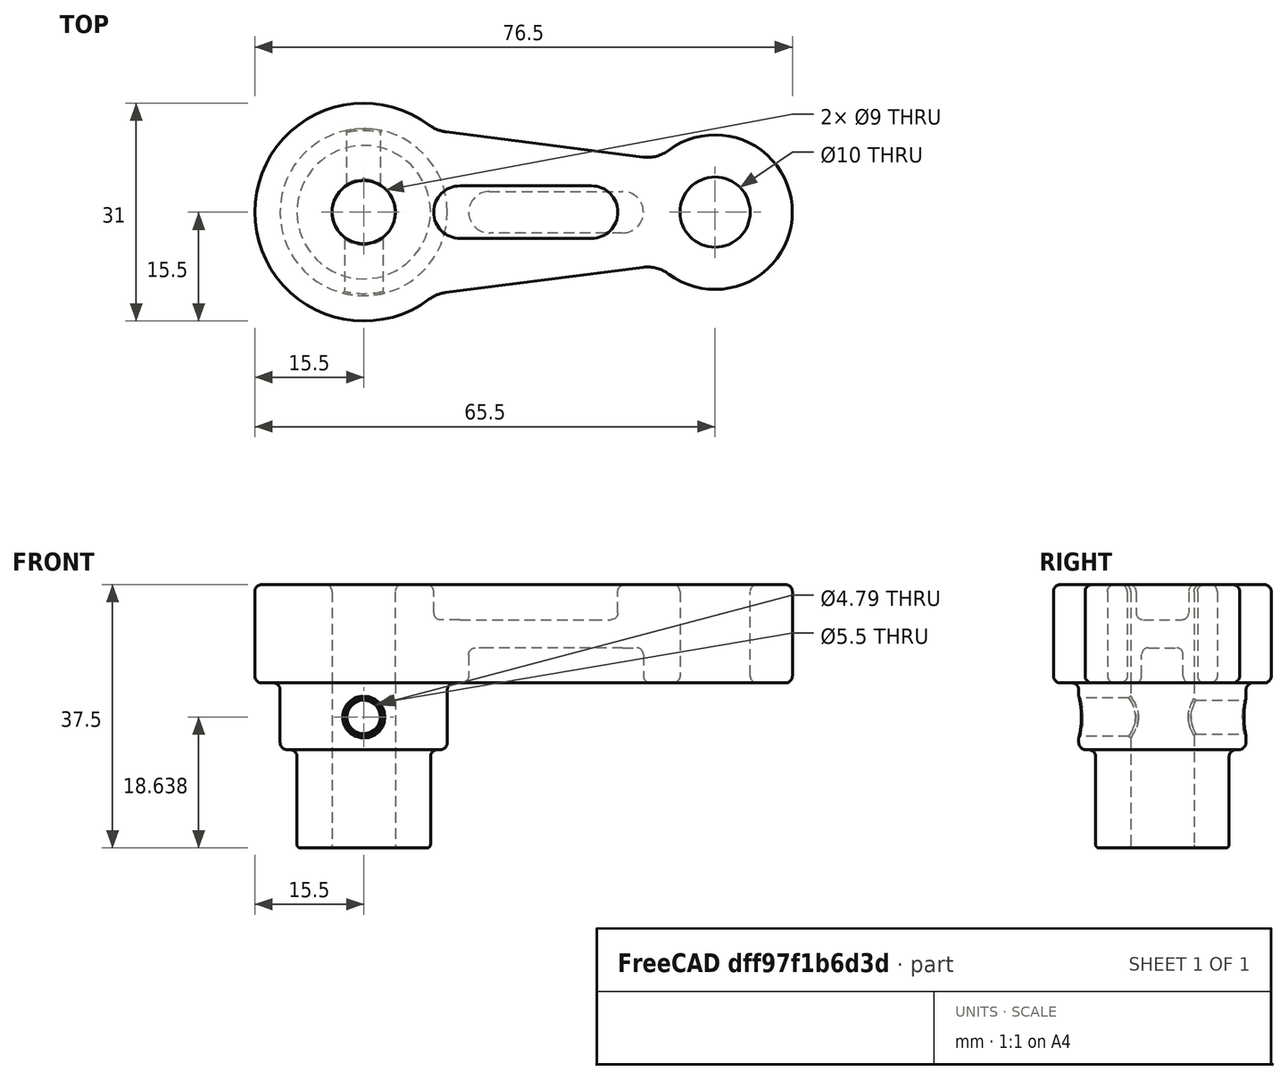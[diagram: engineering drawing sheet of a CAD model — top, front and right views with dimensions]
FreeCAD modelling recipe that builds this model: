
FCSTD DOCUMENT  (FreeCAD 0.19R24291 (Git))
Label: WorkBenchCrank
License: All rights reserved
LicenseURL: http://en.wikipedia.org/wiki/All_rights_reserved
objects: Sketcher::SketchObject×6, PartDesign::Fillet×6, TechDraw::DrawViewDimension×5, TechDraw::DrawProjGroupItem×4, PartDesign::Pad×3, PartDesign::Hole×3, PartDesign::Chamfer×2, PartDesign::Pocket×2, PartDesign::Body×1, TechDraw::DrawSVGTemplate×1, TechDraw::DrawProjGroup×1, TechDraw::DrawPage×1
note: 39 computed .brp shape members not serialized (recipe doc carries the construction recipe); baked Part::Feature solids carry a one-line shape summary decoded from their .brp

FEATURE [Sketcher::SketchObject] Sketch
  FullyConstrained = true
  MapMode = 5
  Support = -> [XY_Plane]
  sketch-geometry (16):
    g0: Circle CenterX=0 CenterY=0 CenterZ=0 NormalX=0 NormalY=0 NormalZ=1 AngleXU=0 Radius=4.5
    g1: ArcOfCircle CenterX=0 CenterY=0 CenterZ=0 NormalX=0 NormalY=0 NormalZ=1 AngleXU=0 Radius=15.5 StartAngle=0.927295 EndAngle=5.35589
    g2: ArcOfCircle CenterX=50 CenterY=0 CenterZ=0 NormalX=0 NormalY=0 NormalZ=1 AngleXU=0 Radius=11 StartAngle=4.06889 EndAngle=8.49748
    g3: GeomPoint X=50 Y=0 Z=0
    g4: Circle CenterX=50 CenterY=0 CenterZ=0 NormalX=0 NormalY=0 NormalZ=1 AngleXU=0 Radius=5
    g5: LineSegment StartX=0 StartY=0 StartZ=0 EndX=50 EndY=0 EndZ=0
    g6: LineSegment StartX=11.6646 StartY=11.4405 StartZ=0 EndX=39.7646 EndY=7.84053 EndZ=0
    g7: LineSegment StartX=39.7646 StartY=-7.84053 StartZ=0 EndX=11.6646 EndY=-11.4405 EndZ=0
    g8: ArcOfCircle CenterX=12.3 CenterY=16.4 CenterZ=0 NormalX=0 NormalY=0 NormalZ=1 AngleXU=0 Radius=5 StartAngle=4.06889 EndAngle=4.58497
    g9: ArcOfCircle CenterX=12.3 CenterY=-16.4 CenterZ=0 NormalX=0 NormalY=0 NormalZ=1 AngleXU=0 Radius=5 StartAngle=1.69822 EndAngle=2.2143
    g10: ArcOfCircle CenterX=40.4 CenterY=12.8 CenterZ=0 NormalX=0 NormalY=0 NormalZ=1 AngleXU=0 Radius=5 StartAngle=4.58497 EndAngle=5.35589
    g11: ArcOfCircle CenterX=40.4 CenterY=-12.8 CenterZ=0 NormalX=0 NormalY=0 NormalZ=1 AngleXU=0 Radius=5 StartAngle=0.927295 EndAngle=1.69822
    g12: LineSegment StartX=12.3 StartY=16.4 StartZ=0 EndX=12.3 EndY=-16.4 EndZ=0
    g13: LineSegment StartX=40.4 StartY=-12.8 StartZ=0 EndX=40.4 EndY=12.8 EndZ=0
    g14: LineSegment StartX=43.4 StartY=8.8 StartZ=0 EndX=43.4 EndY=-8.8 EndZ=0
    g15: LineSegment StartX=9.3 StartY=12.4 StartZ=0 EndX=9.3 EndY=-12.4 EndZ=0
  constraints (36):
    c: Coincident(g0,g-1)
    c: Coincident(g1,g0)
    c: Radius(g0) = 4.5
    c: Radius(g1) = 15.5
    c: Radius(g2) = 11
    c: PointOnObject(g3,g-1)
    c: Coincident(g3,g2)
    c: DistanceX(g0,g2) = 50
    c: Coincident(g4,g2)
    c: Radius(g4) = 5
    c: Coincident(g5,g0)
    c: Coincident(g5,g2)
    c: Tangent(g1,g8) = 1.5708
    c: Tangent(g6,g8) = -1.5708
    c: Tangent(g1,g9) = 1.5708
    c: Tangent(g7,g9) = -1.5708
    c: Tangent(g6,g10) = -1.5708
    c: Tangent(g2,g10) = 1.5708
    c: Tangent(g7,g11) = -1.5708
    c: Tangent(g2,g11) = 1.5708
    c: Equal(g8,g9)
    c: Equal(g9,g11)
    c: Equal(g11,g10)
    c: Radius(g8) = 5
    c: Coincident(g12,g8)
    c: Coincident(g12,g9)
    c: Vertical(g12)
    c: Coincident(g13,g11)
    c: Coincident(g13,g10)
    c: Perpendicular(g13,g5)
    c: Coincident(g14,g2)
    c: Coincident(g14,g2)
    c: DistanceY(g14,g14) = 17.6
    c: Coincident(g15,g1)
    c: Coincident(g15,g1)
    c: DistanceY(g15,g15) = 24.8
FEATURE [PartDesign::Pad] Pad  label="PadCrank"
  Direction = (1,1,1)
  Length = 14
  Length2 = 100
  Profile = -> Sketch
  Type = 0
FEATURE [PartDesign::Fillet] Fillet
  Base = -> Pad [Face12]
  BaseFeature = -> Pad
  Radius = 1
  SupportTransform = false
FEATURE [Sketcher::SketchObject] Sketch001
  FullyConstrained = true
  MapMode = 5
  Support = -> [XY_Plane]
  sketch-geometry (1):
    g0: Circle CenterX=0 CenterY=0 CenterZ=0 NormalX=0 NormalY=0 NormalZ=1 AngleXU=0 Radius=11.9
  constraints (2):
    c: Coincident(g0,g-1)
    c: Radius(g0) = 11.9
FEATURE [PartDesign::Pad] Pad001  label="PadOffset1"
  BaseFeature = -> Fillet
  Direction = (1,1,1)
  Length = 9.5
  Length2 = 100
  Profile = -> Sketch001
  Reversed = true
  Type = 0
FEATURE [PartDesign::Fillet] Fillet001
  Base = -> Pad001 [Face4]
  BaseFeature = -> Pad001
  Radius = 1
  SupportTransform = false
FEATURE [Sketcher::SketchObject] Sketch002
  FullyConstrained = true
  MapMode = 5
  Placement = pos=(0,0,-9.5) rot=(1,0,0;3.14159rad)
  Support = -> [Fillet001]
  sketch-geometry (1):
    g0: Circle CenterX=0 CenterY=0 CenterZ=0 NormalX=0 NormalY=0 NormalZ=1 AngleXU=0 Radius=9.5
  constraints (2):
    c: Coincident(g0,g-1)
    c: Radius(g0) = 9.5
FEATURE [PartDesign::Pad] Pad002  label="PadOFfset2"
  BaseFeature = -> Fillet001
  Direction = (1,1,1)
  Length = 14
  Length2 = 100
  Profile = -> Sketch002
  Type = 0
FEATURE [PartDesign::Fillet] Fillet002
  Base = -> Pad002 [Face34]
  BaseFeature = -> Pad002
  Radius = 1
  SupportTransform = false
FEATURE [PartDesign::Hole] Hole  label="HoleShaft"
  BaseFeature = -> Fillet002
  Depth = 25
  DepthType = 0
  Diameter = 9
  DrillForDepth = false
  DrillPoint = 1
  DrillPointAngle = 118
  HoleCutCountersinkAngle = 90
  HoleCutCustomValues = false
  HoleCutDepth = 0
  HoleCutDiameter = 6.1
  HoleCutType = 0
  ModelActualThread = false
  Profile = -> Sketch001
  Tapered = false
  TaperedAngle = 90
  ThreadAngle = 0
  ThreadClass = 0
  ThreadCutOffInner = 0
  ThreadCutOffOuter = 0
  ThreadDirection = 0
  ThreadFit = 0
  ThreadPitch = 0
  ThreadSize = 0
  ThreadType = 0
  Threaded = false
FEATURE [Sketcher::SketchObject] Sketch003
  FullyConstrained = false
  MapMode = 5
  Placement = pos=(0,0,0) rot=(1,0,0;1.5708rad)
  Support = -> [XZ_Plane]
  sketch-geometry (1):
    g0: Circle CenterX=0 CenterY=-4.86181 CenterZ=0 NormalX=0 NormalY=0 NormalZ=1 AngleXU=0 Radius=4.75
  constraints (2):
    c: PointOnObject(g0,g-2)
    c: Radius(g0) = 4.75  'Roll Pin Hole'
FEATURE [PartDesign::Hole] Hole001  label="HolePin1"
  BaseFeature = -> Hole
  Depth = 12
  DepthType = 0
  Diameter = 4.79
  DrillForDepth = false
  DrillPoint = 1
  DrillPointAngle = 117
  HoleCutCountersinkAngle = 90
  HoleCutCustomValues = false
  HoleCutDepth = 0.1
  HoleCutDiameter = 6.3
  HoleCutType = 2
  ModelActualThread = false
  Profile = -> Sketch003
  Tapered = false
  TaperedAngle = 90
  ThreadAngle = 0
  ThreadClass = 0
  ThreadCutOffInner = 0
  ThreadCutOffOuter = 0
  ThreadDirection = 0
  ThreadFit = 0
  ThreadPitch = 0
  ThreadSize = 0
  ThreadType = 0
  Threaded = false
FEATURE [PartDesign::Hole] Hole002  label="HolePin2"
  BaseFeature = -> Hole001
  Depth = 12
  DepthType = 0
  Diameter = 5.5
  DrillForDepth = false
  DrillPoint = 1
  DrillPointAngle = 118
  HoleCutCountersinkAngle = 90
  HoleCutCustomValues = false
  HoleCutDepth = 0
  HoleCutDiameter = 6.1
  HoleCutType = 0
  ModelActualThread = false
  Profile = -> Sketch003
  Reversed = true
  Tapered = false
  TaperedAngle = 90
  ThreadAngle = 0
  ThreadClass = 0
  ThreadCutOffInner = 0
  ThreadCutOffOuter = 0
  ThreadDirection = 0
  ThreadFit = 0
  ThreadPitch = 0
  ThreadSize = 0
  ThreadType = 0
  Threaded = false
FEATURE [PartDesign::Chamfer] Chamfer
  Angle = 45
  Base = -> Hole002 [Face4]
  BaseFeature = -> Hole002
  ChamferType = 0
  FlipDirection = false
  Size = 0.25
  Size2 = 1
  SupportTransform = false
FEATURE [PartDesign::Chamfer] Chamfer001
  Angle = 45
  Base = -> Chamfer [Face5]
  BaseFeature = -> Chamfer
  ChamferType = 0
  FlipDirection = false
  Size = 0.25
  Size2 = 1
  SupportTransform = false
FEATURE [Sketcher::SketchObject] Sketch004
  FullyConstrained = false
  MapMode = 5
  Placement = pos=(0,0,14) rot=(0,0,1;0rad)
  Support = -> [Chamfer001]
  sketch-geometry (5):
    g0: ArcOfCircle CenterX=13.6958 CenterY=0 CenterZ=0 NormalX=0 NormalY=0 NormalZ=1 AngleXU=0 Radius=3.74416 StartAngle=1.5708 EndAngle=4.71239
    g1: ArcOfCircle CenterX=32.4195 CenterY=-2e-16 CenterZ=0 NormalX=0 NormalY=0 NormalZ=1 AngleXU=0 Radius=3.74416 StartAngle=4.71239 EndAngle=7.85398
    g2: LineSegment StartX=13.6958 StartY=-3.74416 StartZ=0 EndX=32.4195 EndY=-3.74416 EndZ=0
    g3: LineSegment StartX=13.6958 StartY=3.74416 StartZ=0 EndX=32.4195 EndY=3.74416 EndZ=0
    g4: LineSegment StartX=9.95167 StartY=9.60576 StartZ=0 EndX=9.95167 EndY=-10.2092 EndZ=0
  constraints (9):
    c: Tangent(g0,g3) = 1.5708
    c: Tangent(g0,g2) = -1.5708
    c: Tangent(g2,g1) = -1.5708
    c: Tangent(g3,g1) = 1.5708
    c: Horizontal(g2)
    c: Equal(g0,g1)
    c: PointOnObject(g0,g-1)
    c: Vertical(g4)
    c: Tangent(g4,g0)
FEATURE [PartDesign::Pocket] Pocket  label="PocketTopRelief"
  BaseFeature = -> Chamfer001
  Length = 5
  Length2 = 100
  Profile = -> Sketch004
  Type = 0
FEATURE [Sketcher::SketchObject] Sketch005
  FullyConstrained = false
  MapMode = 5
  Placement = pos=(0,0,0) rot=(1,0,0;3.14159rad)
  Support = -> [Pocket]
  sketch-geometry (4):
    g0: ArcOfCircle CenterX=36.8542 CenterY=0 CenterZ=0 NormalX=0 NormalY=0 NormalZ=1 AngleXU=0 Radius=2.95256 StartAngle=4.71239 EndAngle=7.85398
    g1: ArcOfCircle CenterX=17.8823 CenterY=1e-16 CenterZ=0 NormalX=0 NormalY=0 NormalZ=1 AngleXU=0 Radius=2.95256 StartAngle=1.5708 EndAngle=4.71239
    g2: LineSegment StartX=36.8542 StartY=2.95256 StartZ=0 EndX=17.8823 EndY=2.95256 EndZ=0
    g3: LineSegment StartX=36.8542 StartY=-2.95256 StartZ=0 EndX=17.8823 EndY=-2.95256 EndZ=0
  constraints (7):
    c: Tangent(g0,g3) = 1.5708
    c: Tangent(g0,g2) = -1.5708
    c: Tangent(g2,g1) = -1.5708
    c: Tangent(g3,g1) = 1.5708
    c: Horizontal(g2)
    c: Equal(g0,g1)
    c: PointOnObject(g0,g-1)
FEATURE [PartDesign::Pocket] Pocket001  label="PocketBottomRelief"
  BaseFeature = -> Pocket
  Length = 5
  Length2 = 100
  Profile = -> Sketch005
  Type = 0
FEATURE [PartDesign::Fillet] Fillet003
  Base = -> Pocket001 [Face54,Face53,Face51,Face52]
  BaseFeature = -> Pocket001
  Radius = 1
  SupportTransform = false
FEATURE [PartDesign::Fillet] Fillet004
  Base = -> Fillet003 [Face51,Face52,Face53,Face50]
  BaseFeature = -> Fillet003
  Radius = 1
  SupportTransform = false
FEATURE [PartDesign::Fillet] Fillet005
  Base = -> Fillet004 [Face70]
  BaseFeature = -> Fillet004
  Radius = 0.5
  SupportTransform = false
FEATURE [PartDesign::Body] Body
  Group = -> [Sketch,Pad,Fillet,Sketch001,Pad001,Fillet001,Sketch002,Pad002,Fillet002,Hole,Sketch003,Hole001,Hole002,Chamfer,Chamfer001,Sketch004,Pocket,Sketch005,Pocket001,Fillet003,Fillet004,Fillet005]
  Origin = -> Origin
  Tip = -> Fillet005
FEATURE [TechDraw::DrawSVGTemplate] Template
  EditableTexts = Approved1=Approved 1; Approved2=Approved 2; CheckedBy=Checked By; Code=Code; CompanyAddress=3433 Ridgeway Trail, Maryville TN 37801; CompanyName=Amused Scientist; DrawingNumber=Drawing Number; DrawingTitle1=WorkBenchCrank; DrawingTitle2=Drawing Title 2; DrawingTitle3=Drawing Title 3; DrawnBy=Lee Erickson; Revision=Rev; Scale=Scale 1:1; Sheet=Sheet n of m
  Height = 215.9
  Orientation = 1
  Width = 279.4
FEATURE [TechDraw::DrawProjGroupItem] ProjItem001  label="FrontTopRight"
  CoarseView = false
  Direction = (0.57735,0.57735,0.57735)
  Focus = 100
  HardHidden = false
  IsoCount = 0
  IsoHidden = false
  IsoVisible = false
  LockPosition = true
  Perspective = false
  Rotation = 0
  RotationVector = (1,0,0)
  ScaleType = 2
  SeamHidden = false
  SeamVisible = true
  SmoothHidden = false
  SmoothVisible = true
  Source = -> [Body]
  Type = 7
  X = 144.682
  XDirection = (0.707107,0,-0.707107)
  Y = 64.848
FEATURE [TechDraw::DrawProjGroupItem] ProjItem002  label="Bottom"
  CoarseView = false
  Direction = (0,-1,0)
  Focus = 100
  HardHidden = false
  IsoCount = 0
  IsoHidden = false
  IsoVisible = false
  LockPosition = true
  Perspective = false
  Rotation = 0
  RotationVector = (1,0,0)
  ScaleType = 2
  SeamHidden = false
  SeamVisible = true
  SmoothHidden = false
  SmoothVisible = true
  Source = -> [Body]
  Type = 5
  X = 0
  XDirection = (1,0,0)
  Y = 60.1288
FEATURE [TechDraw::DrawProjGroupItem] ProjItem003  label="Right"
  CoarseView = false
  Direction = (1,0,1e-16)
  Focus = 100
  HardHidden = false
  IsoCount = 0
  IsoHidden = false
  IsoVisible = false
  LockPosition = true
  Perspective = false
  Rotation = 0
  RotationVector = (1,0,0)
  ScaleType = 2
  SeamHidden = false
  SeamVisible = true
  SmoothHidden = false
  SmoothVisible = true
  Source = -> [Body]
  Type = 2
  X = 117.665
  XDirection = (1e-16,0,-1)
  Y = 0
FEATURE [TechDraw::DrawProjGroupItem] ProjItem  label="Front"
  CoarseView = false
  Direction = (0,0,1)
  Focus = 100
  HardHidden = false
  IsoCount = 0
  IsoHidden = false
  IsoVisible = false
  LockPosition = true
  Perspective = false
  Rotation = 0
  RotationVector = (1,0,0)
  ScaleType = 2
  SeamHidden = false
  SeamVisible = true
  SmoothHidden = false
  SmoothVisible = true
  Source = -> [Body]
  Type = 0
  X = 0
  XDirection = (1,0,0)
  Y = 0
FEATURE [TechDraw::DrawProjGroup] ProjGroup
  Anchor = -> ProjItem
  AutoDistribute = true
  LockPosition = false
  ProjectionType = 0
  Rotation = 0
  ScaleType = 0
  Source = -> [Body]
  Views = -> [ProjItem,ProjItem001,ProjItem002,ProjItem003]
  X = 69.6773
  Y = 87.5
  spacingX = 15
  spacingY = 15
FEATURE [TechDraw::DrawViewDimension] Dimension
  Arbitrary = false
  ArbitraryTolerances = false
  EqualTolerance = true
  FormatSpec = ⌀%.2f
  FormatSpecOverTolerance = %+.2f
  FormatSpecUnderTolerance = %+.2f
  Inverted = false
  LockPosition = false
  MeasureType = 1
  OverTolerance = 0
  References2D = -> [ProjItem]
  Rotation = 0
  ScaleType = 0
  TheoreticalExact = false
  Type = 5
  UnderTolerance = 0
  X = 46.4582
  Y = 20.9628
FEATURE [TechDraw::DrawViewDimension] Dimension001
  Arbitrary = false
  ArbitraryTolerances = false
  EqualTolerance = true
  FormatSpec = ⌀%.2f
  FormatSpecOverTolerance = %+.2f
  FormatSpecUnderTolerance = %+.2f
  Inverted = false
  LockPosition = false
  MeasureType = 1
  OverTolerance = 0
  References2D = -> [ProjItem]
  Rotation = 0
  ScaleType = 0
  TheoreticalExact = false
  Type = 5
  UnderTolerance = 0
  X = -36.4017
  Y = 26.6285
FEATURE [TechDraw::DrawViewDimension] Dimension002
  Arbitrary = false
  ArbitraryTolerances = false
  EqualTolerance = true
  FormatSpec = %.2f
  FormatSpecOverTolerance = %+.2f
  FormatSpecUnderTolerance = %+.2f
  Inverted = false
  LockPosition = false
  MeasureType = 1
  OverTolerance = 0
  References2D = -> [ProjItem002]
  Rotation = 0
  ScaleType = 0
  TheoreticalExact = false
  Type = 2
  UnderTolerance = 0
  X = 50.8913
  Y = 13.1723
FEATURE [TechDraw::DrawViewDimension] Dimension003
  Arbitrary = false
  ArbitraryTolerances = false
  EqualTolerance = true
  FormatSpec = ⌀%.2f
  FormatSpecOverTolerance = %+.2f
  FormatSpecUnderTolerance = %+.2f
  Inverted = false
  LockPosition = false
  MeasureType = 1
  OverTolerance = 0
  References2D = -> [ProjItem]
  Rotation = 0
  ScaleType = 0
  TheoreticalExact = false
  Type = 5
  UnderTolerance = 0
  X = 51.817
  Y = 11.5673
FEATURE [TechDraw::DrawViewDimension] Dimension004
  Arbitrary = false
  ArbitraryTolerances = false
  EqualTolerance = true
  FormatSpec = ⌀%.2f
  FormatSpecOverTolerance = %+.2f
  FormatSpecUnderTolerance = %+.2f
  Inverted = false
  LockPosition = false
  MeasureType = 1
  OverTolerance = 0
  References2D = -> [ProjItem]
  Rotation = 0
  ScaleType = 0
  TheoreticalExact = false
  Type = 5
  UnderTolerance = 0
  X = 54.0596
  Y = 0.59017
FEATURE [TechDraw::DrawPage] Page  label="PageCrankDrawing"
  KeepUpdated = true
  NextBalloonIndex = 1
  ProjectionType = 0
  Template = -> Template
  Views = -> [ProjGroup,Dimension,Dimension001,Dimension002,Dimension003,Dimension004]
